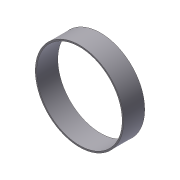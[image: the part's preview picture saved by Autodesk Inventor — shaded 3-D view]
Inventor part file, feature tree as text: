
AUTODESK INVENTOR PART (.ipt)
format: ipt  version: 2012 (Build 160160000, 160)  size: 80,896 bytes
history: native  units: in
note: dims shown in document units (in); Inventor stores cm internally (conversion verified against a paired STEP export)
features: extrude x1, sketch x1
ambient origin geometry x8: Origin, YZ Plane, XZ Plane, XY Plane, X Axis, Y Axis, Z Axis, Center Point
bodies: Solid1 (feature_tree)
feature tree (2):
  extrude  "Extrusion1"  Depth=0.125in
  sketch  "Sketch1"  dims[d0=7.1in d1=0.125in d2=1.75in d3=0.0in]
